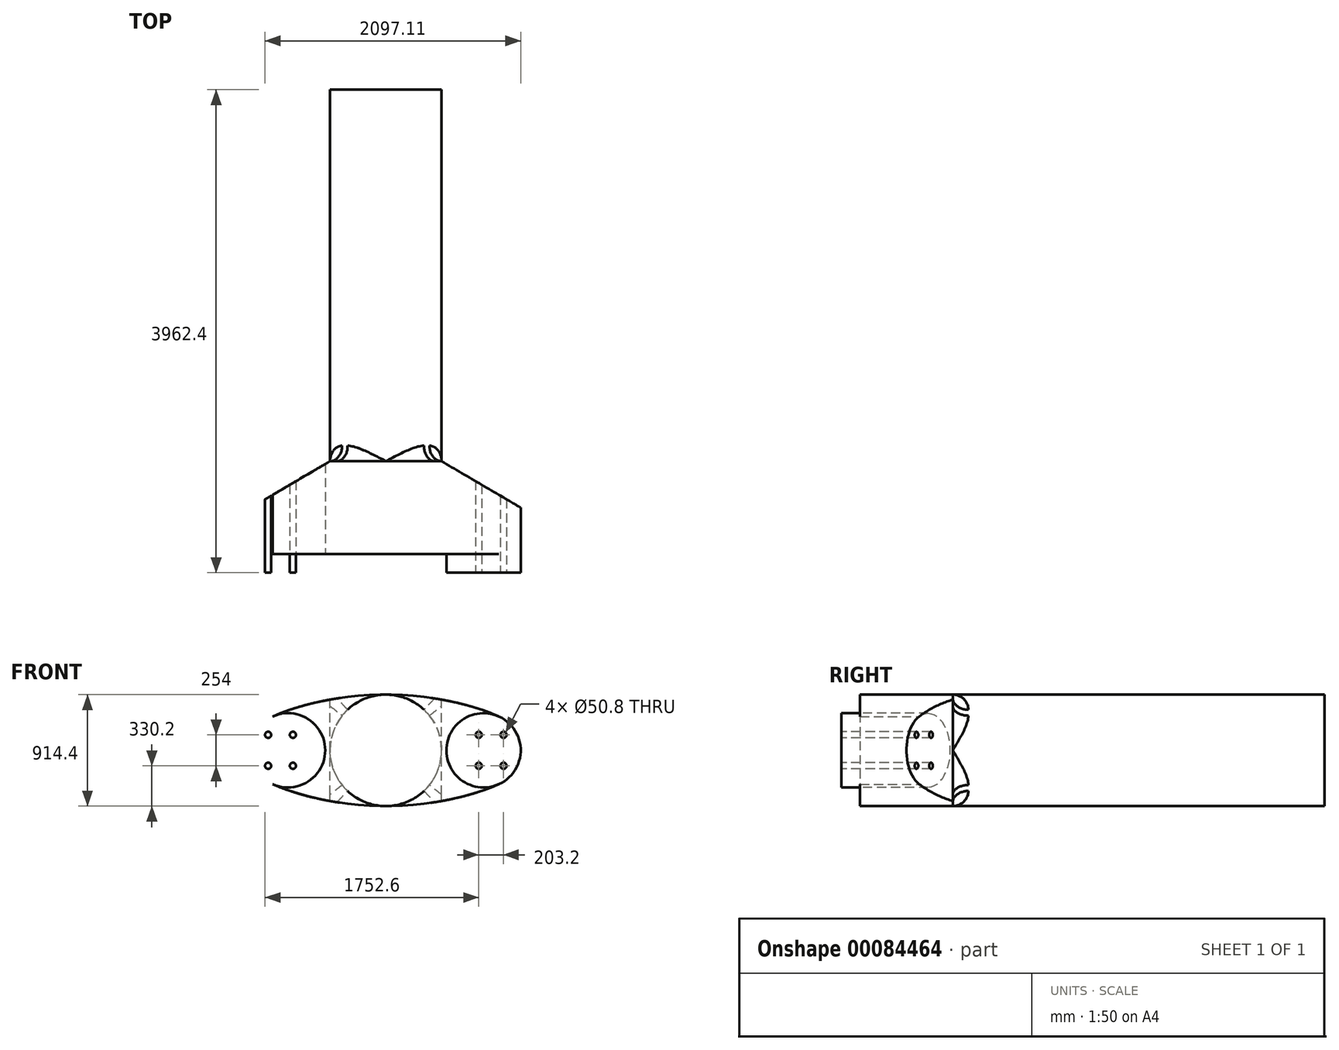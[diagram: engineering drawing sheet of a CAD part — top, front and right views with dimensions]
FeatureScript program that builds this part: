
annotation { "Feature Type Name" : "Feature", "Feature Type Description" : "" }
export const myFeature = defineFeature(function(context is Context, id is Id, definition is map)
    precondition{}
    {
        {
            var Q0;
            Q0=qCreatedBy(makeId("Front.planeOp"),FACE);
            var sketch = newSketch(context, id + "F0", { "sketchPlane" : qUnion([Q0])});
            skCircle(sketch, "E0", {"center": v(0, 0) * mm, "radius": 457.2 * mm});
            skSolve(sketch);
        }
        {
            var Q0;
            Q0=makeQuery(id+"F0.imprint","IMPRINT",FACE,{"disambiguationData":[TD([[makeQuery(id+"F0.imprint","IMPRINT",EDGE,{"derivedFrom":sQuery(id+"F0.wireOp",EDGE,"E0")}),1.0]])]});
            extrude(context, id + "F1", {"entities" : qUnion([Q0]), "depth" : 3048 * mm});
        }
        {
            var Q0;
            Q0=makeQuery(id+"F1.opExtrude","CAP_FACE",FACE,{"disambiguationData":[OSD([sQuery(id+"F0.wireOp",EDGE,"E0")])],"isStart":false});
            var sketch = newSketch(context, id + "F2", { "sketchPlane" : qUnion([Q0])});
            skArc(sketch, "E1", {"start": v(-926.8, 277.95) * mm, "mid": v(-1106.5, 0) * mm, "end": v(-926.8, -277.95) * mm});
            skArc(sketch, "E2", {"start": v(926.8, -277.95) * mm, "mid": v(1106.5, 0) * mm, "end": v(926.8, 277.95) * mm});
            skLineSegment(sketch, "E3", {"start": v(-1910.57, 0) * mm, "end": v(2370.63, 0) * mm, "construction": true});
            skFitSpline(sketch, "E4", {"points": [v(-1219.2, 0) * mm, v(0, 457.2) * mm, v(1219.2, 0) * mm, v(0, -457.2) * mm, v(-1219.2, 0) * mm]});
            skSolve(sketch);
        }
        {
            var Q0;
            {var subQ0=sQuery(id+"F2.wireOp",EDGE,"E1");Q0=makeQuery(id+"F2.imprint","IMPRINT",FACE,{"disambiguationData":[TD([[makeQuery(id+"F2.imprint","IMPRINT",EDGE,{"derivedFrom":subQ0}),1.0]])]});}
            var Q1;
            {var subQ0=makeQuery(id+"F1.opExtrude","CAP_EDGE",EDGE,{"disambiguationData":[OSD([sQuery(id+"F0.wireOp",EDGE,"E0")])],"isStart":false});var subQ1=makeQuery(id+"F2.imprint","INTERSECT",VERTEX,{"derivedFrom":[subQ0,sQuery(id+"F2.wireOp",EDGE,"E4")]});Q1=makeQuery(id+"F2.imprint","IMPRINT",FACE,{"disambiguationData":[TD([[makeQuery(id+"F2.imprint","IMPRINT",EDGE,{"disambiguationData":[TD([[subQ1,1.0]])],"derivedFrom":subQ0}),1.0]])]});}
            var Q2;
            {var subQ0=sQuery(id+"F2.wireOp",EDGE,"E2");Q2=makeQuery(id+"F2.imprint","IMPRINT",FACE,{"disambiguationData":[TD([[makeQuery(id+"F2.imprint","IMPRINT",EDGE,{"derivedFrom":subQ0}),1.0]])]});}
            extrude(context, id + "F3", {"entities" : qUnion([Q0, Q1, Q2]), "operationType" : NewBodyOperationType.ADD, "depth" : 762 * mm});
        }
        {
            var Q0;
            Q0=qCreatedBy(makeId("Top.planeOp"),FACE);
            var sketch = newSketch(context, id + "F4", { "sketchPlane" : qUnion([Q0])});
            skFitSpline(sketch, "E5.1", {"points": [v(-926.8, -3048) * mm, v(-617.86, -3048) * mm, v(-308.93, -3048) * mm, v(0, -3048) * mm]});
            skFitSpline(sketch, "E5.2", {"points": [v(0, -3048) * mm, v(308.93, -3048) * mm, v(617.86, -3048) * mm, v(926.8, -3048) * mm]});
            skLineSegment(sketch, "E5.7", {"start": v(1106.5, -3048) * mm, "end": v(926.8, -3048) * mm});
            skLineSegment(sketch, "E5.8", {"start": v(-926.8, -3048) * mm, "end": v(-1106.5, -3048) * mm});
            skLineSegment(sketch, "E6.0", {"start": v(457.2, -3048) * mm, "end": v(0, -3048) * mm});
            skLineSegment(sketch, "E6.1", {"start": v(0, -3048) * mm, "end": v(-457.2, -3048) * mm});
            skLineSegment(sketch, "E7", {"start": v(1238.04, -3429) * mm, "end": v(-1693.48, -3429) * mm, "construction": true});
            skPoint(sketch, "E7.startSnap0", {"position": v(926.8, -3429) * mm});
            skLineSegment(sketch, "E8", {"start": v(-457.2, -3048) * mm, "end": v(-1106.5, -3429) * mm});
            skLineSegment(sketch, "E9", {"start": v(457.2, -3048) * mm, "end": v(1106.5, -3429) * mm});
            skLineSegment(sketch, "E10", {"start": v(-1106.5, -3810) * mm, "end": v(-1106.5, -3048) * mm});
            skLineSegment(sketch, "E11", {"start": v(1106.5, -3810) * mm, "end": v(1106.5, -3048) * mm});
            skSolve(sketch);
        }
        {
            var Q0;
            Q0 = qSketchRegion(id + "F4", true);
            extrude(context, id + "F5", {"entities" : qUnion([Q0]), "operationType" : NewBodyOperationType.REMOVE, "endBound" : BoundingType.SYMMETRIC, "oppositeDirection" : true, "depth" : 914.4 * mm});
        }
        {
            var Q0;
            {var subQ0=sQuery(id+"F0.wireOp",EDGE,"E0");var subQ1=sQuery(id+"F2.wireOp",EDGE,"E4");Q0=makeQuery(id+"F5.boolean.opBoolean","SPLIT",EDGE,{"disambiguationData":[TD([makeQuery(id+"F3.opExtrude","SWEPT_FACE",FACE,{"disambiguationData":[OSD([subQ1])]})])],"derivedFrom":makeQuery(id+"F3.boolean.opBoolean","SPLIT",EDGE,{"disambiguationData":[OD(1.0)],"derivedFrom":makeQuery(id+"F1.opExtrude","CAP_EDGE",EDGE,{"disambiguationData":[OSD([subQ0])],"isStart":false})})});}
            fillet(context, id + "F6", {"entities" : qUnion([Q0]), "radius" : 127 * mm, "tangentPropagation" : true, "allowEdgeOverflow" : false});
        }
        {
            var Q0;
            Q0=makeQuery(id+"F3.opExtrude","CAP_FACE",FACE,{"disambiguationData":[OSD([sQuery(id+"F2.wireOp",EDGE,"E1"),sQuery(id+"F2.wireOp",EDGE,"E2"),sQuery(id+"F2.wireOp",EDGE,"E4"),sQuery(id+"F2.wireOp",EDGE,"E4")])],"isStart":false});
            var sketch = newSketch(context, id + "F7", { "sketchPlane" : qUnion([Q0])});
            skCircle(sketch, "E12", {"center": v(801.7, 0) * mm, "radius": 304.8 * mm});
            skCircle(sketch, "E13", {"center": v(-801.7, 0) * mm, "radius": 304.8 * mm});
            skSolve(sketch);
        }
        {
            var Q0;
            {var subQ0=sQuery(id+"F7.wireOp",EDGE,"E12");var subQ1=makeQuery(id+"F7.imprint","INTERSECT",VERTEX,{"derivedFrom":[makeQuery(id+"F3.opExtrude","CAP_EDGE",EDGE,{"disambiguationData":[OSD([sQuery(id+"F2.wireOp",EDGE,"E4")])],"isStart":false}),subQ0]});Q0=makeQuery(id+"F7.imprint","IMPRINT",FACE,{"disambiguationData":[TD([[makeQuery(id+"F7.imprint","IMPRINT",EDGE,{"disambiguationData":[TD([[subQ1,-1.0]])],"derivedFrom":subQ0}),1.0]])]});}
            var Q1;
            {var subQ0=sQuery(id+"F7.wireOp",EDGE,"E13");var subQ1=makeQuery(id+"F7.imprint","INTERSECT",VERTEX,{"derivedFrom":[makeQuery(id+"F3.opExtrude","CAP_EDGE",EDGE,{"disambiguationData":[OSD([sQuery(id+"F2.wireOp",EDGE,"E4")])],"isStart":false}),subQ0]});Q1=makeQuery(id+"F7.imprint","IMPRINT",FACE,{"disambiguationData":[TD([[makeQuery(id+"F7.imprint","IMPRINT",EDGE,{"disambiguationData":[TD([[subQ1,-1.0]])],"derivedFrom":subQ0}),1.0]])]});}
            extrude(context, id + "F8", {"entities" : qUnion([Q0, Q1]), "operationType" : NewBodyOperationType.ADD, "depth" : 152.4 * mm});
        }
        {
            var Q0;
            Q0=makeQuery(id+"F8.opExtrude","CAP_FACE",FACE,{"disambiguationData":[OSD([sQuery(id+"F7.wireOp",EDGE,"E12")])],"isStart":false});
            var sketch = newSketch(context, id + "F9", { "sketchPlane" : qUnion([Q0])});
            skFitSpline(sketch, "E14.0", {"points": [v(-1219.2, 0) * mm, v(-1219.2, 228.6) * mm, v(0, 685.8) * mm, v(1828.8, 0) * mm, v(0, -685.8) * mm, v(-1219.2, -228.6) * mm, v(-1219.2, 0) * mm]});
            skFitSpline(sketch, "E14.1", {"points": [v(-1219.2, 0) * mm, v(-1219.2, 228.6) * mm, v(0, 685.8) * mm, v(1828.8, 0) * mm, v(0, -685.8) * mm, v(-1219.2, -228.6) * mm, v(-1219.2, 0) * mm]});
            skCircle(sketch, "E14.2", {"center": v(801.7, 0) * mm, "radius": 304.8 * mm});
            skCircle(sketch, "E14.3", {"center": v(-801.7, 0) * mm, "radius": 304.8 * mm});
            skLineSegment(sketch, "E15", {"start": v(801.7, 0) * mm, "end": v(-801.7, 0) * mm, "construction": true});
            skLineSegment(sketch, "E16", {"start": v(0, -457.2) * mm, "end": v(0, 457.2) * mm, "construction": true});
            skPoint(sketch, "E16.startSnap0", {"position": v(0, 0) * mm});
            skCircle(sketch, "E17", {"center": v(762, -127) * mm, "radius": 25.4 * mm});
            skCircle(sketch, "E18", {"center": v(762, 127) * mm, "radius": 25.4 * mm});
            skCircle(sketch, "E19", {"center": v(965.2, -127) * mm, "radius": 25.4 * mm});
            skCircle(sketch, "E20", {"center": v(965.2, 127) * mm, "radius": 25.4 * mm});
            skCircle(sketch, "E21.MirrorC", {"center": v(-762, -127) * mm, "radius": 25.4 * mm});
            skCircle(sketch, "E22.MirrorC", {"center": v(-965.2, -127) * mm, "radius": 25.4 * mm});
            skCircle(sketch, "E23.MirrorC", {"center": v(-965.2, 127) * mm, "radius": 25.4 * mm});
            skCircle(sketch, "E24.MirrorC", {"center": v(-762, 127) * mm, "radius": 25.4 * mm});
            skSolve(sketch);
        }
        {
            var Q0;
            Q0=makeQuery(id+"F9.imprint","IMPRINT",FACE,{"disambiguationData":[TD([[makeQuery(id+"F9.imprint","IMPRINT",EDGE,{"derivedFrom":sQuery(id+"F9.wireOp",EDGE,"E19")}),1.0]])]});
            var Q1;
            Q1=makeQuery(id+"F9.imprint","IMPRINT",FACE,{"disambiguationData":[TD([[makeQuery(id+"F9.imprint","IMPRINT",EDGE,{"derivedFrom":sQuery(id+"F9.wireOp",EDGE,"E20")}),1.0]])]});
            var Q2;
            Q2=makeQuery(id+"F9.imprint","IMPRINT",FACE,{"disambiguationData":[TD([[makeQuery(id+"F9.imprint","IMPRINT",EDGE,{"derivedFrom":sQuery(id+"F9.wireOp",EDGE,"E18")}),1.0]])]});
            var Q3;
            Q3=makeQuery(id+"F9.imprint","IMPRINT",FACE,{"disambiguationData":[TD([[makeQuery(id+"F9.imprint","IMPRINT",EDGE,{"derivedFrom":sQuery(id+"F9.wireOp",EDGE,"E17")}),1.0]])]});
            var Q4;
            Q4=makeQuery(id+"F9.imprint","IMPRINT",FACE,{"disambiguationData":[TD([[makeQuery(id+"F9.imprint","IMPRINT",EDGE,{"derivedFrom":sQuery(id+"F9.wireOp",EDGE,"E24.MirrorC")}),-1.0]])]});
            var Q5;
            Q5=makeQuery(id+"F9.imprint","IMPRINT",FACE,{"disambiguationData":[TD([[makeQuery(id+"F9.imprint","IMPRINT",EDGE,{"derivedFrom":sQuery(id+"F9.wireOp",EDGE,"E23.MirrorC")}),-1.0]])]});
            var Q6;
            Q6=makeQuery(id+"F9.imprint","IMPRINT",FACE,{"disambiguationData":[TD([[makeQuery(id+"F9.imprint","IMPRINT",EDGE,{"derivedFrom":sQuery(id+"F9.wireOp",EDGE,"E22.MirrorC")}),-1.0]])]});
            var Q7;
            Q7=makeQuery(id+"F9.imprint","IMPRINT",FACE,{"disambiguationData":[TD([[makeQuery(id+"F9.imprint","IMPRINT",EDGE,{"derivedFrom":sQuery(id+"F9.wireOp",EDGE,"E21.MirrorC")}),-1.0]])]});
            extrude(context, id + "F10", {"entities" : qUnion([Q0, Q1, Q2, Q3, Q4, Q5, Q6, Q7]), "operationType" : NewBodyOperationType.REMOVE, "endBound" : BoundingType.THROUGH_ALL, "oppositeDirection" : true, "depth" : 25.4 * mm});
        }
    });
